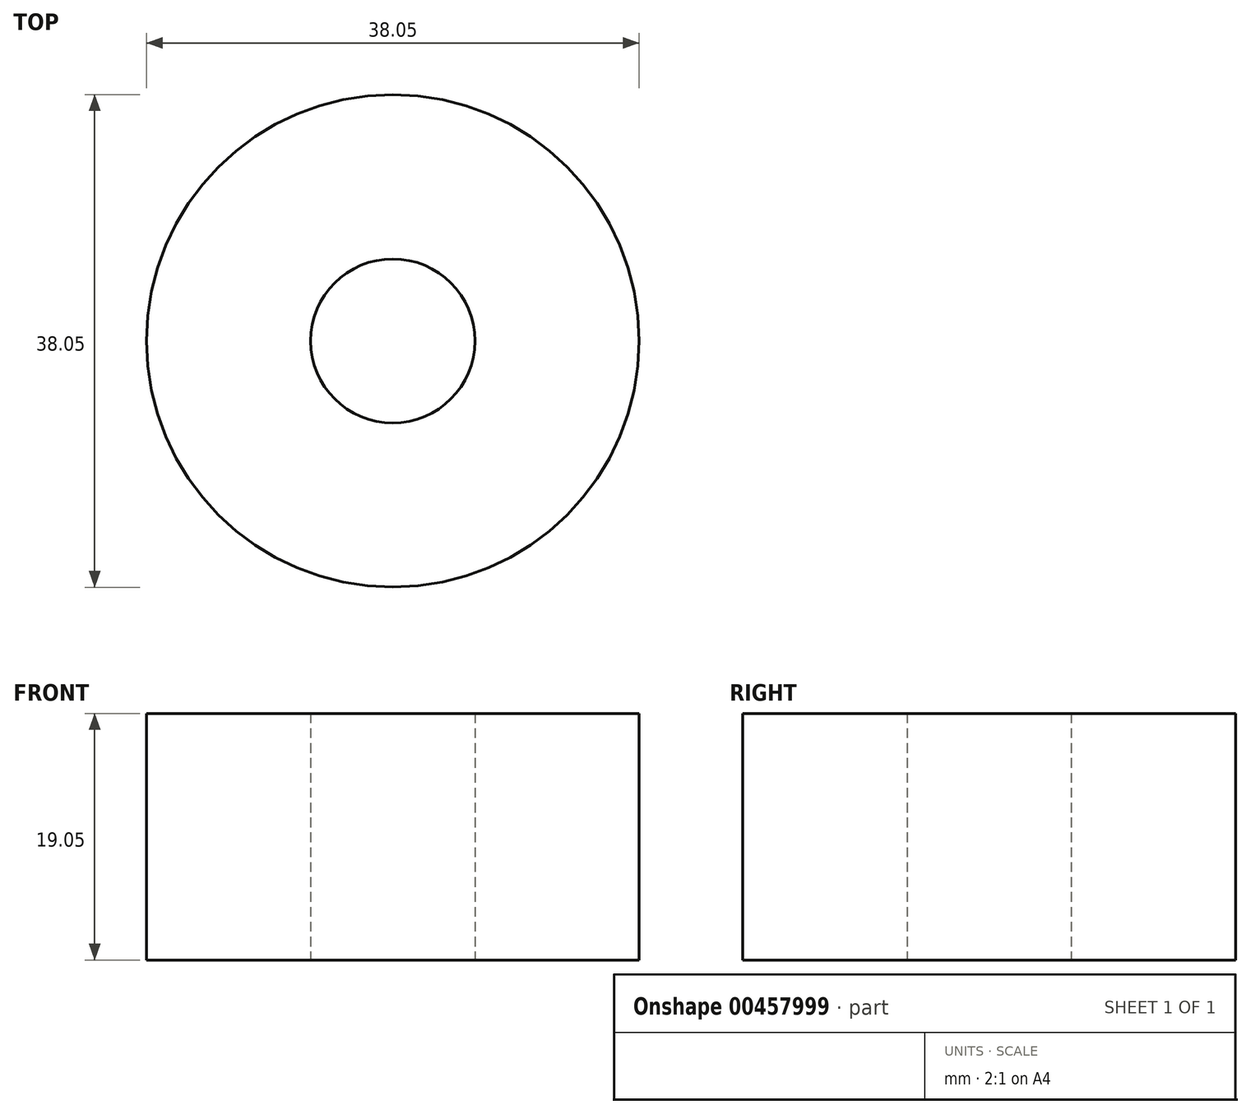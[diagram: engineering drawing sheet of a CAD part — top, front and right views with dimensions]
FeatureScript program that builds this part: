
annotation { "Feature Type Name" : "Feature", "Feature Type Description" : "" }
export const myFeature = defineFeature(function(context is Context, id is Id, definition is map)
    precondition{}
    {
        {
            var Q0;
            Q0=qCreatedBy(makeId("Top.planeOp"),FACE);
            var sketch = newSketch(context, id + "F0", { "sketchPlane" : qUnion([Q0])});
            skCircle(sketch, "E0", {"center": v(0.2, 41.08) * mm, "radius": 19.02 * mm});
            skCircle(sketch, "E1", {"center": v(0.2, 41.08) * mm, "radius": 6.34 * mm});
            skSolve(sketch);
        }
        {
            var Q0;
            Q0=makeQuery(id+"F0.imprint","IMPRINT",FACE,{"disambiguationData":[TD([[makeQuery(id+"F0.imprint","IMPRINT",EDGE,{"derivedFrom":sQuery(id+"F0.wireOp",EDGE,"E0")}),1.0]])]});
            extrude(context, id + "F1", {"entities" : qUnion([Q0]), "depth" : 19.05 * mm});
        }
    });
